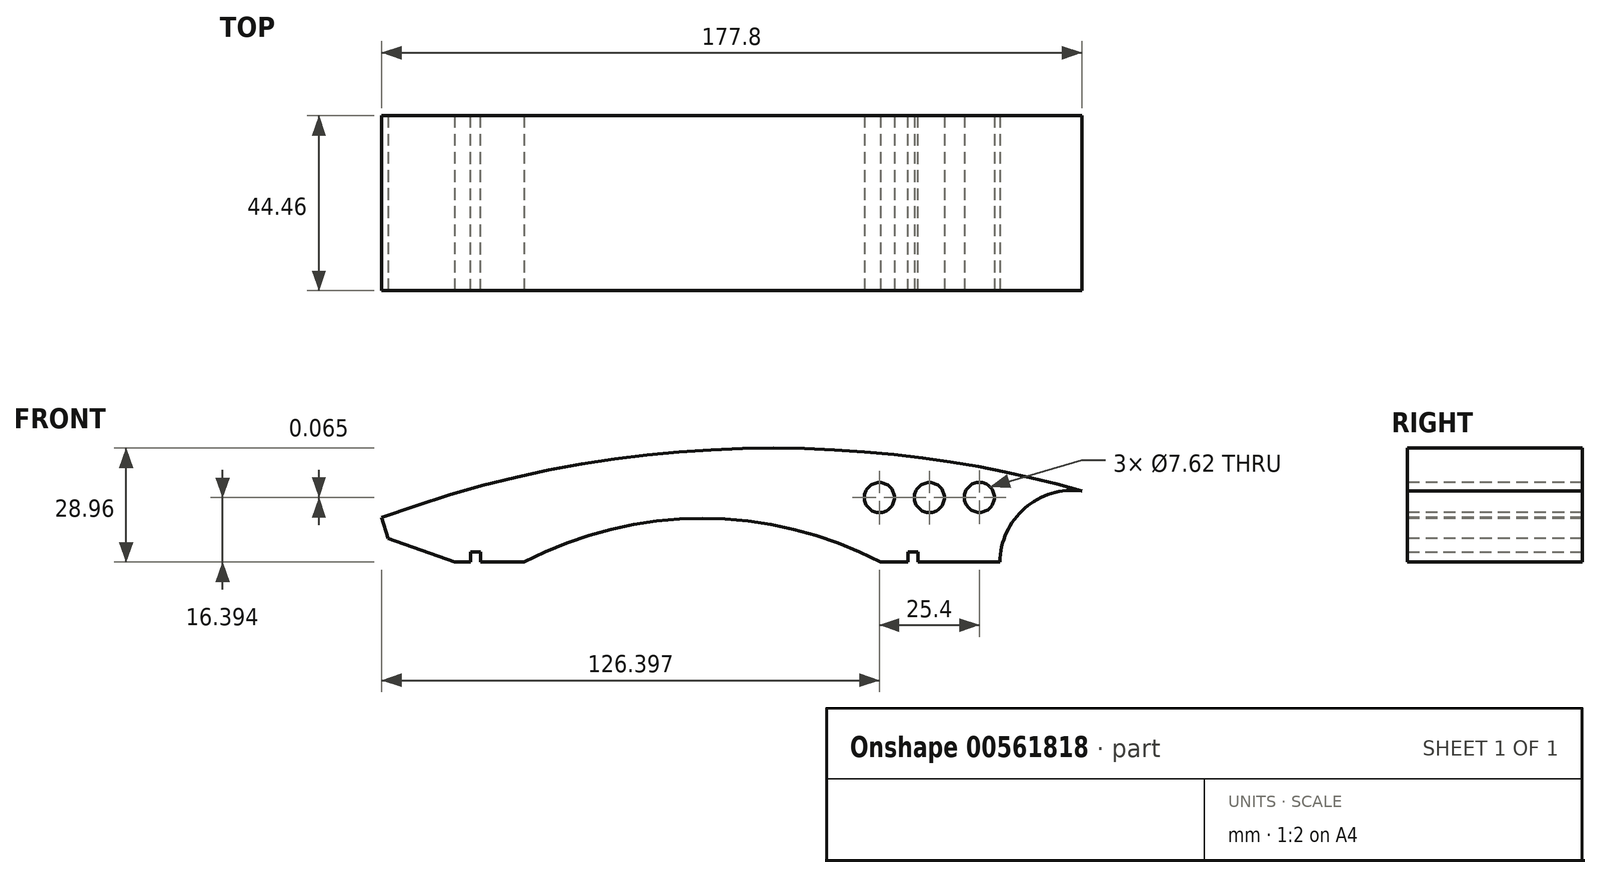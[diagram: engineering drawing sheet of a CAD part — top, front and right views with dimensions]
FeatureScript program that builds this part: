
annotation { "Feature Type Name" : "Feature", "Feature Type Description" : "" }
export const myFeature = defineFeature(function(context is Context, id is Id, definition is map)
    precondition{}
    {
        {
            var Q0;
            Q0=qCreatedBy(makeId("Front.planeOp"),FACE);
            var sketch = newSketch(context, id + "F0", { "sketchPlane" : qUnion([Q0])});
            skLineSegment(sketch, "E0.bottom", {"start": v(-88.9, -15.88) * mm, "end": v(88.9, -15.88) * mm});
            skLineSegment(sketch, "E0.top", {"start": v(-88.9, 15.88) * mm, "end": v(88.9, 15.88) * mm});
            skLineSegment(sketch, "E0.left", {"start": v(-88.9, -15.88) * mm, "end": v(-88.9, 15.88) * mm});
            skLineSegment(sketch, "E0.right", {"start": v(88.9, -15.88) * mm, "end": v(88.9, 15.88) * mm});
            skLineSegment(sketch, "E1", {"start": v(-88.9, 15.88) * mm, "end": v(88.9, -15.88) * mm, "construction": true});
            skPoint(sketch, "E2", {"position": v(0, 0) * mm});
            skSolve(sketch);
        }
        {
            var Q0;
            Q0=makeQuery(id+"F0.imprint","IMPRINT",FACE,{"disambiguationData":[TD([[makeQuery(id+"F0.imprint","IMPRINT",EDGE,{"derivedFrom":sQuery(id+"F0.wireOp",EDGE,"E0.bottom")}),1.0]])]});
            extrude(context, id + "F5", {"entities" : qUnion([Q0]), "endBound" : BoundingType.SYMMETRIC, "depth" : 44.45 * mm});
        }
        {
            var Q0;
            Q0=qCreatedBy(makeId("Front.planeOp"),FACE);
            var sketch = newSketch(context, id + "F1", { "sketchPlane" : qUnion([Q0])});
            skLineSegment(sketch, "E3.0", {"start": v(-88.9, -15.88) * mm, "end": v(88.9, -15.88) * mm, "construction": true});
            skLineSegment(sketch, "E4.bottom", {"start": v(-66.36, -15.88) * mm, "end": v(-63.82, -15.88) * mm});
            skLineSegment(sketch, "E4.top", {"start": v(-66.36, -13.34) * mm, "end": v(-63.82, -13.34) * mm});
            skLineSegment(sketch, "E4.left", {"start": v(-66.36, -15.88) * mm, "end": v(-66.36, -13.34) * mm});
            skLineSegment(sketch, "E4.right", {"start": v(-63.82, -15.88) * mm, "end": v(-63.82, -13.34) * mm});
            skLineSegment(sketch, "E5.bottom", {"start": v(44.77, -15.88) * mm, "end": v(47.3, -15.88) * mm});
            skLineSegment(sketch, "E5.top", {"start": v(44.77, -13.34) * mm, "end": v(47.3, -13.34) * mm});
            skLineSegment(sketch, "E5.left", {"start": v(44.77, -15.88) * mm, "end": v(44.77, -13.34) * mm});
            skLineSegment(sketch, "E5.right", {"start": v(47.3, -15.88) * mm, "end": v(47.3, -13.34) * mm});
            skPoint(sketch, "E6", {"position": v(-65.09, -15.88) * mm});
            skPoint(sketch, "E7", {"position": v(46.04, -15.88) * mm});
            skSolve(sketch);
        }
        {
            var Q0;
            Q0=qSketchRegion(id+"F1",true);
            extrude(context, id + "F2", {"entities" : qUnion([Q0]), "operationType" : NewBodyOperationType.REMOVE, "endBound" : BoundingType.UP_TO_NEXT, "depth" : 50.8 * mm, "hasSecondDirection" : true, "secondDirectionBound" : SecondDirectionBoundingType.UP_TO_NEXT, "secondDirectionOppositeDirection" : true, "secondDirectionDepth" : 25.4 * mm});
        }
        {
            var Q0;
            Q0=makeQuery(id+"F5.opExtrude","CAP_FACE",FACE,{"disambiguationData":[OSD([sQuery(id+"F0.wireOp",EDGE,"E0.bottom"),sQuery(id+"F0.wireOp",EDGE,"E0.top"),sQuery(id+"F0.wireOp",EDGE,"E0.left"),sQuery(id+"F0.wireOp",EDGE,"E0.right")])],"isStart":false});
            var sketch = newSketch(context, id + "F3", { "sketchPlane" : qUnion([Q0])});
            skLineSegment(sketch, "E8", {"start": v(-88.9, -4.58) * mm, "end": v(-87.29, -9.87) * mm});
            skLineSegment(sketch, "E9", {"start": v(-87.29, -9.87) * mm, "end": v(-70.4, -15.88) * mm});
            skFitSpline(sketch, "E10", {"points": [v(-88.9, -4.58) * mm, v(88.9, 2.23) * mm], "startDerivative": vector(196.12, 72.96) * mm, "endDerivative": vector(142.63, -40.94) * mm});
            skLineSegment(sketch, "E11", {"start": v(-70.4, -15.88) * mm, "end": v(-93.32, -24.5) * mm});
            skLineSegment(sketch, "E12", {"start": v(-93.32, -24.5) * mm, "end": v(-99.3, -4.23) * mm});
            skLineSegment(sketch, "E13", {"start": v(-99.3, -4.23) * mm, "end": v(-91.2, 31.55) * mm});
            skLineSegment(sketch, "E14", {"start": v(-91.2, 31.55) * mm, "end": v(-24.4, 31.55) * mm});
            skLineSegment(sketch, "E15", {"start": v(-24.4, 31.55) * mm, "end": v(84.68, 31.55) * mm});
            skLineSegment(sketch, "E16", {"start": v(84.68, 31.55) * mm, "end": v(95.25, 10.22) * mm});
            skArc(sketch, "E17", {"start": v(88.9, 2.23) * mm, "mid": v(74.45, -2.17) * mm, "end": v(68.1, -15.88) * mm});
            skLineSegment(sketch, "E18", {"start": v(95.25, 10.22) * mm, "end": v(97.06, -13.22) * mm});
            skLineSegment(sketch, "E19", {"start": v(97.06, -13.22) * mm, "end": v(90.89, -24.32) * mm});
            skLineSegment(sketch, "E20", {"start": v(90.89, -24.32) * mm, "end": v(68.1, -15.88) * mm});
            skCircle(sketch, "E21", {"center": v(37.5, 0.51) * mm, "radius": 3.81 * mm});
            skCircle(sketch, "E22", {"center": v(50.2, 0.51) * mm, "radius": 3.81 * mm});
            skCircle(sketch, "E23", {"center": v(62.9, 0.58) * mm, "radius": 3.81 * mm});
            skArc(sketch, "E24", {"start": v(37.8, -15.88) * mm, "mid": v(-7.49, -4.74) * mm, "end": v(-52.78, -15.88) * mm});
            skLineSegment(sketch, "E25", {"start": v(-52.78, -15.87) * mm, "end": v(-8.02, -30.14) * mm});
            skLineSegment(sketch, "E26", {"start": v(-8.02, -30.14) * mm, "end": v(37.8, -15.88) * mm});
            skSolve(sketch);
        }
        {
            var Q0;
            Q0 = qSketchRegion(id + "F3", true);
            extrude(context, id + "F4", {"entities" : qUnion([Q0]), "operationType" : NewBodyOperationType.REMOVE, "oppositeDirection" : true, "depth" : 101.6 * mm, "offsetDistance" : 25.4 * mm});
        }
    });
